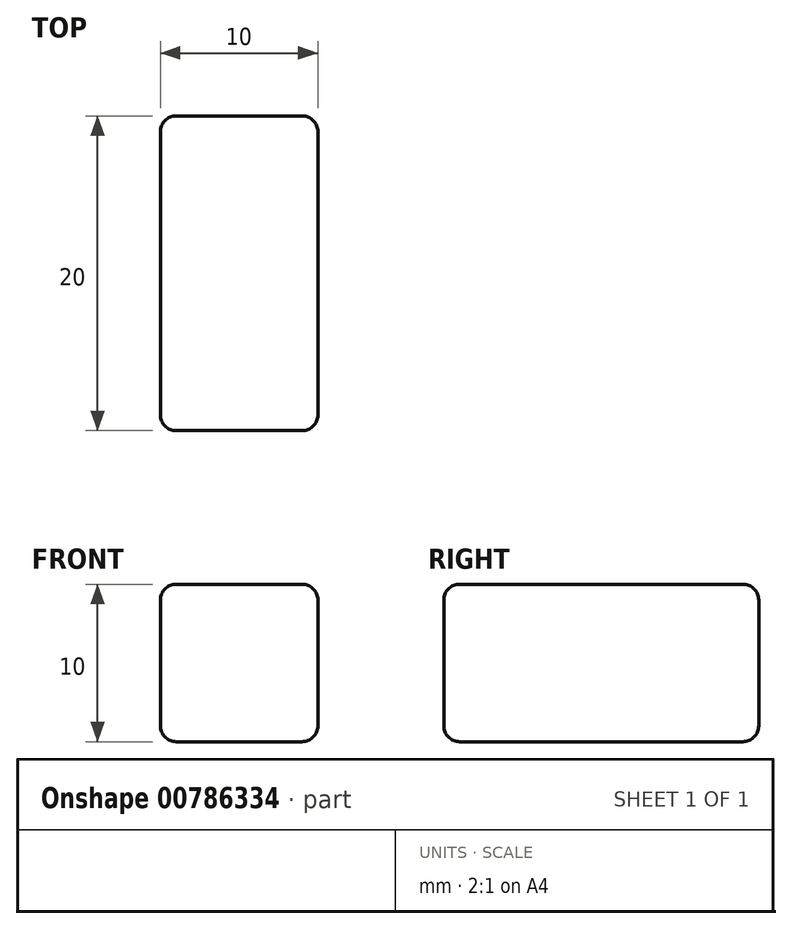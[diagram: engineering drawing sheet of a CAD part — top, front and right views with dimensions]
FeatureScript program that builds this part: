
annotation { "Feature Type Name" : "Feature", "Feature Type Description" : "" }
export const myFeature = defineFeature(function(context is Context, id is Id, definition is map)
    precondition{}
    {
        {
            var Q0;
            Q0=qCreatedBy(makeId("Front.planeOp"),FACE);
            var sketch = newSketch(context, id + "F0", { "sketchPlane" : qUnion([Q0])});
            skLineSegment(sketch, "E0.bottom", {"start": v(0, 0) * mm, "end": v(10, 0) * mm});
            skLineSegment(sketch, "E0.top", {"start": v(0, 10) * mm, "end": v(10, 10) * mm});
            skLineSegment(sketch, "E0.left", {"start": v(0, 0) * mm, "end": v(0, 10) * mm});
            skLineSegment(sketch, "E0.right", {"start": v(10, 0) * mm, "end": v(10, 10) * mm});
            skSolve(sketch);
        }
        {
            var Q0;
            Q0=makeQuery(id+"F0.imprint","IMPRINT",FACE,{"disambiguationData":[TD([[makeQuery(id+"F0.imprint","IMPRINT",EDGE,{"derivedFrom":sQuery(id+"F0.wireOp",EDGE,"E0.bottom")}),1.0]])]});
            extrude(context, id + "F1", {"entities" : qUnion([Q0]), "oppositeDirection" : true, "depth" : 20 * mm, "offsetDistance" : 25.4 * mm});
        }
        {
            var Q0;
            Q0=makeQuery(id+"F1.opExtrude","CAP_FACE",FACE,{"disambiguationData":[OSD([sQuery(id+"F0.wireOp",EDGE,"E0.bottom"),sQuery(id+"F0.wireOp",EDGE,"E0.top"),sQuery(id+"F0.wireOp",EDGE,"E0.left"),sQuery(id+"F0.wireOp",EDGE,"E0.right")])],"isStart":true});
            var Q1;
            Q1=makeQuery(id+"F1.opExtrude","SWEPT_FACE",FACE,{"disambiguationData":[OSD([sQuery(id+"F0.wireOp",EDGE,"E0.right")])]});
            var Q2;
            Q2=makeQuery(id+"F1.opExtrude","SWEPT_FACE",FACE,{"disambiguationData":[OSD([sQuery(id+"F0.wireOp",EDGE,"E0.top")])]});
            var Q3;
            Q3=makeQuery(id+"F1.opExtrude","CAP_FACE",FACE,{"disambiguationData":[OSD([sQuery(id+"F0.wireOp",EDGE,"E0.bottom"),sQuery(id+"F0.wireOp",EDGE,"E0.top"),sQuery(id+"F0.wireOp",EDGE,"E0.left"),sQuery(id+"F0.wireOp",EDGE,"E0.right")])],"isStart":false});
            var Q4;
            Q4=makeQuery(id+"F1.opExtrude","SWEPT_FACE",FACE,{"disambiguationData":[OSD([sQuery(id+"F0.wireOp",EDGE,"E0.left")])]});
            fillet(context, id + "F2", {"entities" : qUnion([Q0, Q1, Q2, Q3, Q4]), "radius" : 1 * mm, "tangentPropagation" : true, "allowEdgeOverflow" : false});
        }
    });
